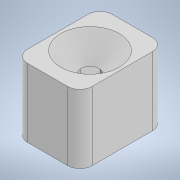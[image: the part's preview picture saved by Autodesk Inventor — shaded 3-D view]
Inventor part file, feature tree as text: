
AUTODESK INVENTOR PART (.ipt)
format: ipt  version: 2022 (Build 260153000, 153)  size: 144,896 bytes
history: native  units: mm
features: sketch x3, extrude x3, other x1, fillet x1, chamfer x1
ambient origin geometry x8: Origin, YZ Plane, XZ Plane, XY Plane, X Axis, Y Axis, Z Axis, Center Point
bodies: Body1 (feature_tree)
feature tree (9):
  other  "솔리드1"
  sketch  "스케치1"
  extrude  "돌출2"  Depth=21.0mm
  extrude  "돌출3"  Depth=4.5mm
  extrude  "돌출4"  Depth=12.0mm TaperAngle=0.0deg
  sketch  "스케치2"
  sketch  "스케치3"
  fillet  "모깎기1"  Radius=5.0mm
  chamfer  "모따기1"  Distance=13.0mm
